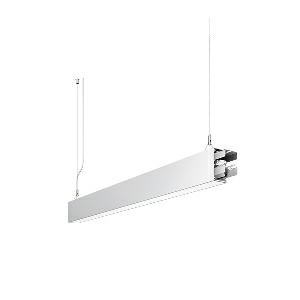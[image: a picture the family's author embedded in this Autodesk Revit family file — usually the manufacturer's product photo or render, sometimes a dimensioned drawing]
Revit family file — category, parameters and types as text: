
# Revit family: idoo_line_-_ilp_2000_vtl_d_sta_00806444_485d
name_source: partatom
category: Lighting Fixtures
units: mm (PartAtom-declared; Revit-internal decimal feet)

## family parameters
Cut with Voids When Loaded = No
Host = Face
Light Source = No
Part Type = Normal
Room Calculation Point = No
Round Connector Dimension = Use Diameter
Shared = No

## types (1)
- IDOO.line - ILP 2000/VTL/D STA (1 x LED, 2300 lm, 2700-6500K)
    Apparent Load = 23 VA
    Approval mark = CE
    CIE Flux Codes = 66 91 98 40 100
    Color Rendering = 90-100
    Color Temperature = 2700-6500K
    Control Gear = Electronic ballast
    Default Elevation = 1800 mm
    Description = ILP 2000/VTL/D|Suspended luminaire|light source: LED|connected load: 220-240 V, 50/60 Hz|Power consumption: approx. 23 W|standby: approx. 0,25|luminous flux: 2300 lm|luminous efficacy: 100 lm/W|light distribution: Direct/indirect|direct ratio: approx. 40 %|colour temperature: Cold white, ca. 2700-6500 K|color rendering index (CRI): >= 90|chromaticity tolerance:  3 SDCM|System of protection: IP 40|technology: Continuously dimmable|luminaire body|material: Sectional aluminium|colour: White|lamp cover: Acrylic (PMMA), Clear|mains lead: 2.00 m With free stranded wires|Fastening: Steel cable 0.3 - 0.7 m|glare control: Prism aperture|luminance(L65): <= 2700 cd/m|unified glare rating(4H 8H): <=  16|special features: Specified values at approx. 4000 K, DALI Load 1x, Through-wired, up to 18 m on one mains connection, External control required for Dali Device type 8, Flicker-free, Constant luminous flux between 2700 and 6500 K, Constant colour temperature over the whole dimming range, Suitable as emergency lighting, Start luminaire with mains connection, Mechanical and electrical connection of the individual modules without tools|
    Frequency = 50 Hz
    Height = 110 mm
    Lamp = 1 x LED
    Lamp Light Flux = 2300 lm
    Lamp count = 1
    Length = 848 mm
    Luminous efficacy = 100 lm/W
    Manufacturer = Waldmann
    ModVariant = No
    Model = 00806444
    Mounting Place = Ceiling
    Mounting Type = Pendant
    Number of Poles = 1
    OnlyDefault = Yes
    Power Factor = 1
    Product Name = IDOO.line - ILP 2000/VTL/D STA
    Product group = Suspended luminaire
    ProductGroupID = 9
    Protection Class = Protection class I
    Protection Degree = IP 40
    RLX_Detail_Level = 1
    RLX_Emergency_Light_Flux = 0 lm
    RLX_Emergency_Type = 0
    RLX_Emergency_Type_DB = No
    RlxData = <blob elided: 19785 chars, md5=b8b06f69>
    Socket = socket
    Standby Power = 0 W
    System Light Flux = 2300 lm
    System Power = 23 W
    Type Comments = Product without accessories
    Type Image = 113295000-00692543.jpg
    URL = http://relux.com
    VarID = ---
    Voltage = 230 V
    Voltage Range = 220-240 V
    Weight = 0.00 kg
    Width = 60 mm  [stored 0.19685 ft]

note: [stored X ft] marks values corroborated as IEEE doubles in the binary element streams (Revit-internal decimal feet)

## geometry (parser evidence)
native form markers: Blend x4, Sweep x14
no freeform markers — native parametric forms only
